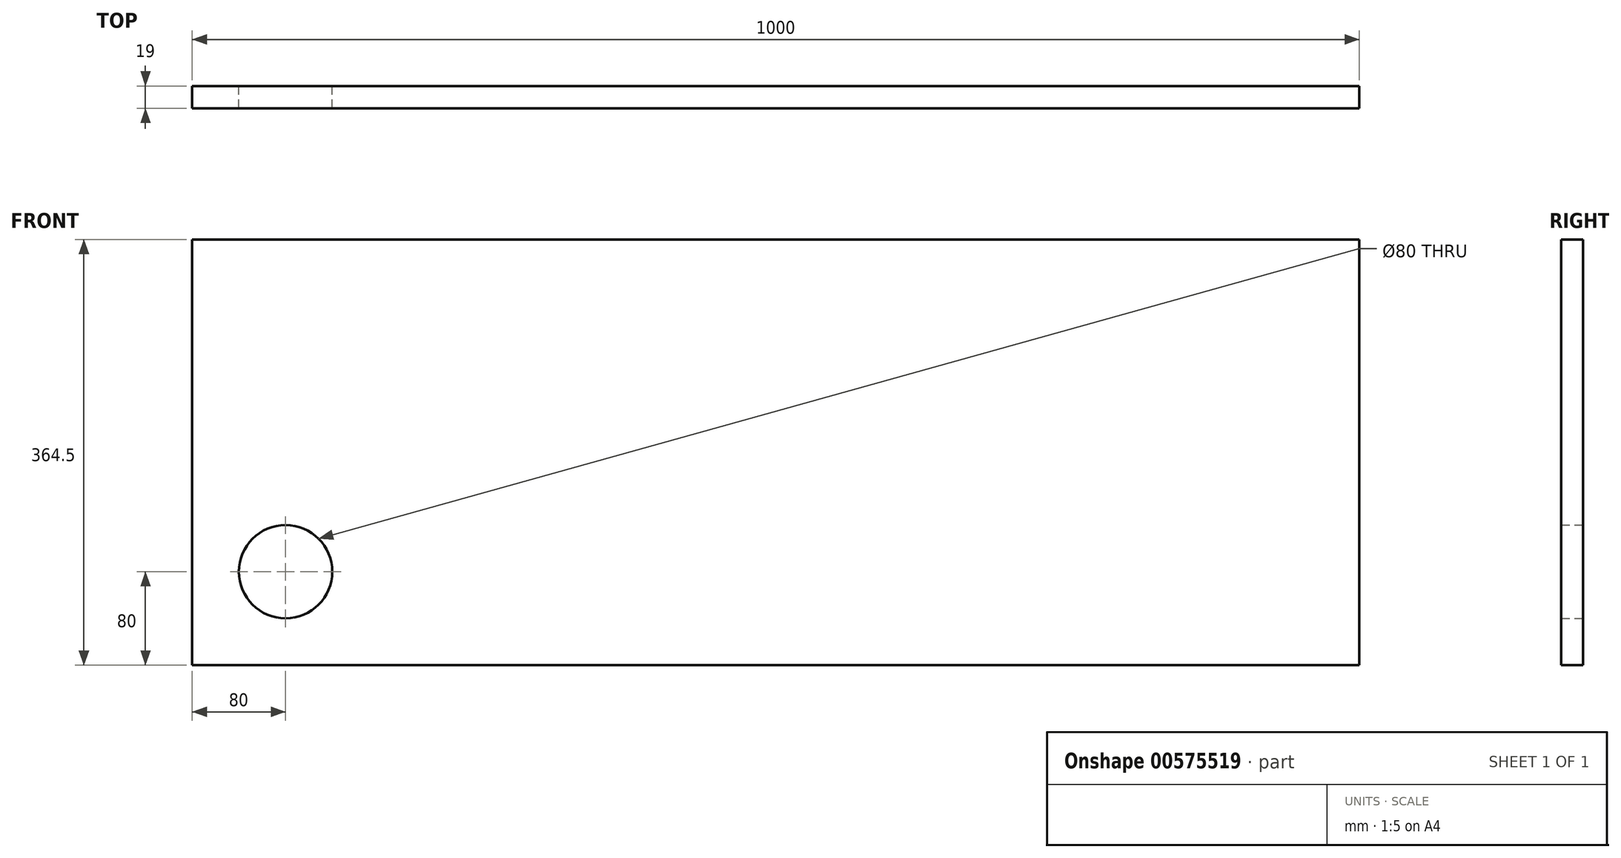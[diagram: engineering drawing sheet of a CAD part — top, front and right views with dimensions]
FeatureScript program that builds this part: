
annotation { "Feature Type Name" : "Feature", "Feature Type Description" : "" }
export const myFeature = defineFeature(function(context is Context, id is Id, definition is map)
    precondition{}
    {
        {
            var Q0;
            Q0=qCreatedBy(makeId("Front.planeOp"),FACE);
            var sketch = newSketch(context, id + "F0", { "sketchPlane" : qUnion([Q0])});
            skLineSegment(sketch, "E0.bottom", {"start": v(0, 0) * mm, "end": v(1000, 0) * mm, "construction": true});
            skLineSegment(sketch, "E0.left", {"start": v(0, 0) * mm, "end": v(0, 1590) * mm, "construction": true});
            skLineSegment(sketch, "E0.right", {"start": v(1000, 0) * mm, "end": v(1000, 1590) * mm, "construction": true});
            skLineSegment(sketch, "E1", {"start": v(500, 1590) * mm, "end": v(500, 0) * mm, "construction": true});
            skLineSegment(sketch, "E2.bottom", {"start": v(0, 1590) * mm, "end": v(1000, 1590) * mm, "construction": true});
            skLineSegment(sketch, "E2.left", {"start": v(0, 1590) * mm, "end": v(0, 290) * mm, "construction": true});
            skSolve(sketch);
        }
        {
            var Q0;
            Q0=qCreatedBy(makeId("Front.planeOp"),FACE);
            var sketch = newSketch(context, id + "F1", { "sketchPlane" : qUnion([Q0])});
            skLineSegment(sketch, "E3.bottom", {"start": v(0, 25) * mm, "end": v(1000, 25) * mm});
            skLineSegment(sketch, "E3.top", {"start": v(0, 389.5) * mm, "end": v(1000, 389.5) * mm});
            skLineSegment(sketch, "E3.left", {"start": v(0, 25) * mm, "end": v(0, 389.5) * mm});
            skLineSegment(sketch, "E3.right", {"start": v(1000, 25) * mm, "end": v(1000, 389.5) * mm});
            skLineSegment(sketch, "E4", {"start": v(0, 25) * mm, "end": v(1000, 25) * mm, "construction": true});
            skCircle(sketch, "E5", {"center": v(80, 105) * mm, "radius": 40 * mm});
            skSolve(sketch);
        }
        {
            var Q0;
            Q0=makeQuery(id+"F1.imprint","IMPRINT",FACE,{"disambiguationData":[TD([[makeQuery(id+"F1.imprint","IMPRINT",EDGE,{"derivedFrom":sQuery(id+"F1.wireOp",EDGE,"E3.bottom")}),1.0]])]});
            extrude(context, id + "F2", {"entities" : qUnion([Q0]), "depth" : 19 * mm, "offsetDistance" : 25 * mm});
        }
        {
            var Q0;
            Q0=makeQuery(id+"F2.opExtrude","SWEPT_BODY",BODY,{"disambiguationData":[OSD([sQuery(id+"F1.wireOp",EDGE,"E3.bottom"),sQuery(id+"F1.wireOp",EDGE,"E3.top"),sQuery(id+"F1.wireOp",EDGE,"E3.left"),sQuery(id+"F1.wireOp",EDGE,"E3.right"),sQuery(id+"F1.wireOp",EDGE,"E5")])]});
            var Q1;
            Q1=makeQuery(id+"F2.opExtrude","CAP_VERTEX",VERTEX,{"disambiguationData":[OSD([sQuery(id+"F1.wireOp",EDGE,"E3.bottom"),sQuery(id+"F1.wireOp",EDGE,"E3.left")])],"isStart":true});
            var Q2;
            Q2=sQuery(id+"F0.wireOp",VERTEX,"E0.bottom.start");
            transform(context, id + "F3", {"entities" : qUnion([Q0]), "transformType" : TransformType.TRANSLATION_ENTITY, "oppositeDirectionEntity" : false, "transformLine" : qUnion([Q1, Q2]), "makeCopy" : false});
        }
    });
